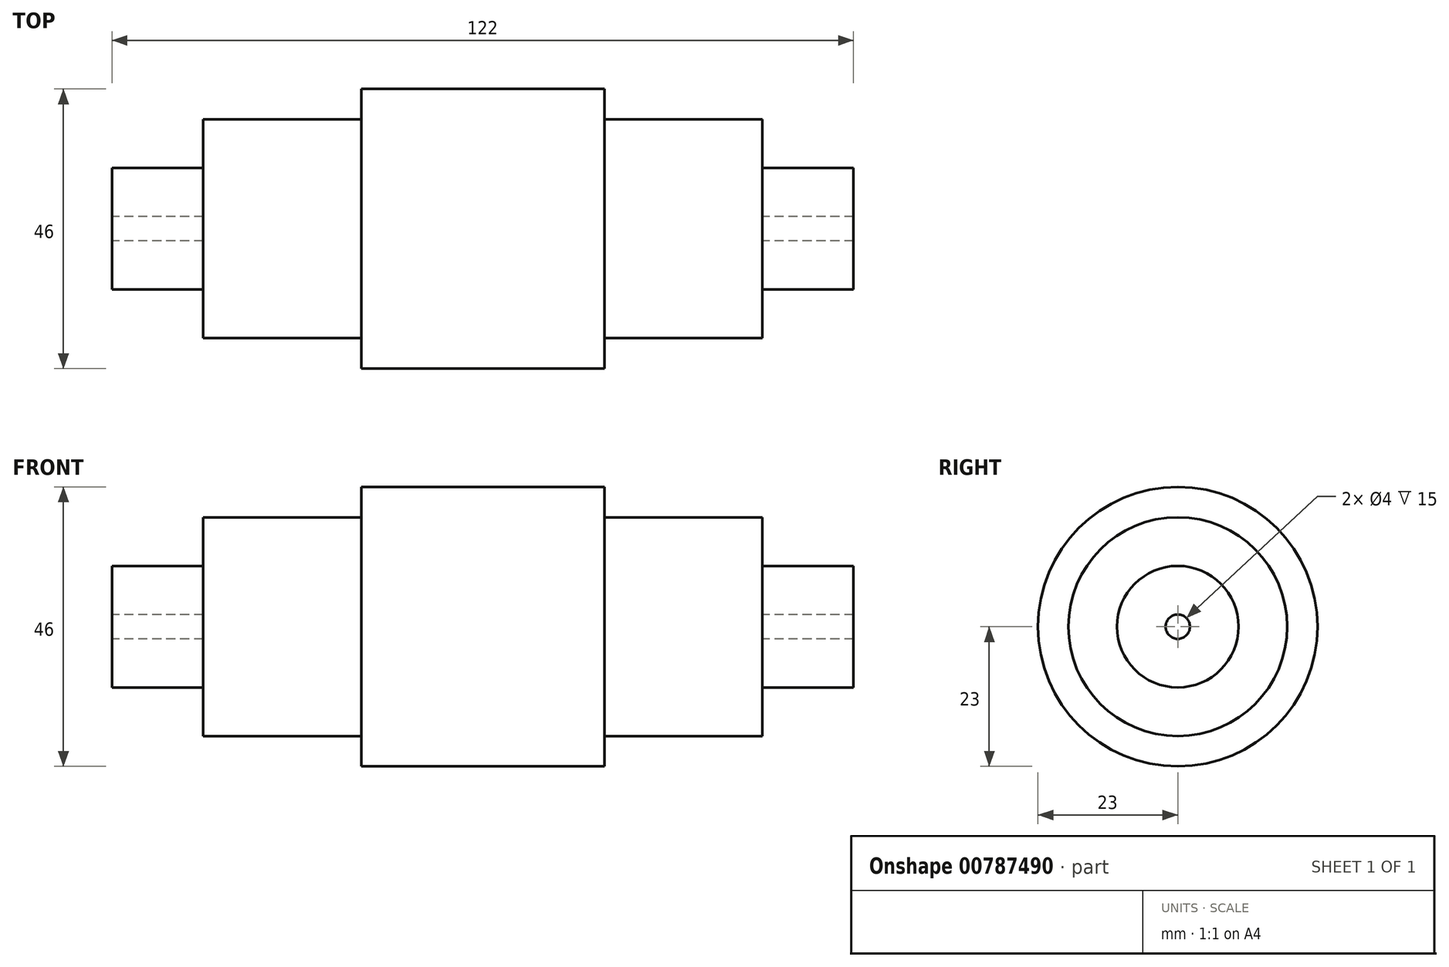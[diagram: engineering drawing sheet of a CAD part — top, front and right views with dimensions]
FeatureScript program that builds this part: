
annotation { "Feature Type Name" : "Feature", "Feature Type Description" : "" }
export const myFeature = defineFeature(function(context is Context, id is Id, definition is map)
    precondition{}
    {
        {
            var Q0;
            Q0=qCreatedBy(makeId("Front.planeOp"),FACE);
            var sketch = newSketch(context, id + "F0", { "sketchPlane" : qUnion([Q0])});
            skLineSegment(sketch, "E0.bottom", {"start": v(-20, 0) * mm, "end": v(38.07, 0) * mm});
            skLineSegment(sketch, "E0.top", {"start": v(-20, 23) * mm, "end": v(20, 23) * mm});
            skLineSegment(sketch, "E0.left", {"start": v(-20, 18) * mm, "end": v(-20, 23) * mm});
            skLineSegment(sketch, "E1.bottom", {"start": v(-46, 0) * mm, "end": v(46, 0) * mm});
            skLineSegment(sketch, "E1.top", {"start": v(-46, 18) * mm, "end": v(-20, 18) * mm});
            skLineSegment(sketch, "E1.left", {"start": v(-46, 0) * mm, "end": v(-46, 2) * mm});
            skLineSegment(sketch, "E1.right", {"start": v(46, 0) * mm, "end": v(46, 2) * mm});
            skPoint(sketch, "E2.oppositeSnap0", {"position": v(-20, 11.5) * mm});
            skLineSegment(sketch, "E2.bottom", {"start": v(-61, 2) * mm, "end": v(-46, 2) * mm});
            skLineSegment(sketch, "E2.top", {"start": v(-61, 10) * mm, "end": v(-46, 10) * mm});
            skLineSegment(sketch, "E2.left", {"start": v(-61, 2) * mm, "end": v(-61, 10) * mm});
            skLineSegment(sketch, "E3.trimOffspring", {"start": v(-46, 10) * mm, "end": v(-46, 18) * mm});
            skLineSegment(sketch, "E4.trimOffspring", {"start": v(46, 2) * mm, "end": v(61, 2) * mm});
            skLineSegment(sketch, "E5.trimOffspring", {"start": v(20, 18) * mm, "end": v(46, 18) * mm});
            skLineSegment(sketch, "E6.trimOffspring", {"start": v(20, 18) * mm, "end": v(20, 23) * mm});
            skLineSegment(sketch, "E7.trimOffspring", {"start": v(46, 10) * mm, "end": v(46, 18) * mm});
            skLineSegment(sketch, "E8", {"start": v(-71.56, 0) * mm, "end": v(66.75, 0) * mm, "construction": true});
            skPoint(sketch, "E2.right.end.orphan", {"position": v(61, 11.5) * mm});
            skLineSegment(sketch, "E9", {"start": v(46, 10) * mm, "end": v(61, 10) * mm});
            skLineSegment(sketch, "E10", {"start": v(61, 10) * mm, "end": v(61, 2) * mm});
            skSolve(sketch);
        }
        {
            var Q0;
            Q0=makeQuery(id+"F0.imprint","IMPRINT",FACE,{"disambiguationData":[TD([[makeQuery(id+"F0.imprint","IMPRINT",EDGE,{"derivedFrom":sQuery(id+"F0.wireOp",EDGE,"E0.top")}),-1.0]])]});
            var Q1;
            Q1=sQuery(id+"F0.wireOp",EDGE,"E8");
            revolve(context, id + "F1", {"surfaceOperationType" : NewSurfaceOperationType.NEW, "entities" : qUnion([Q0]), "axis" : qUnion([Q1]), "revolveType" : RevolveType.FULL});
        }
    });
